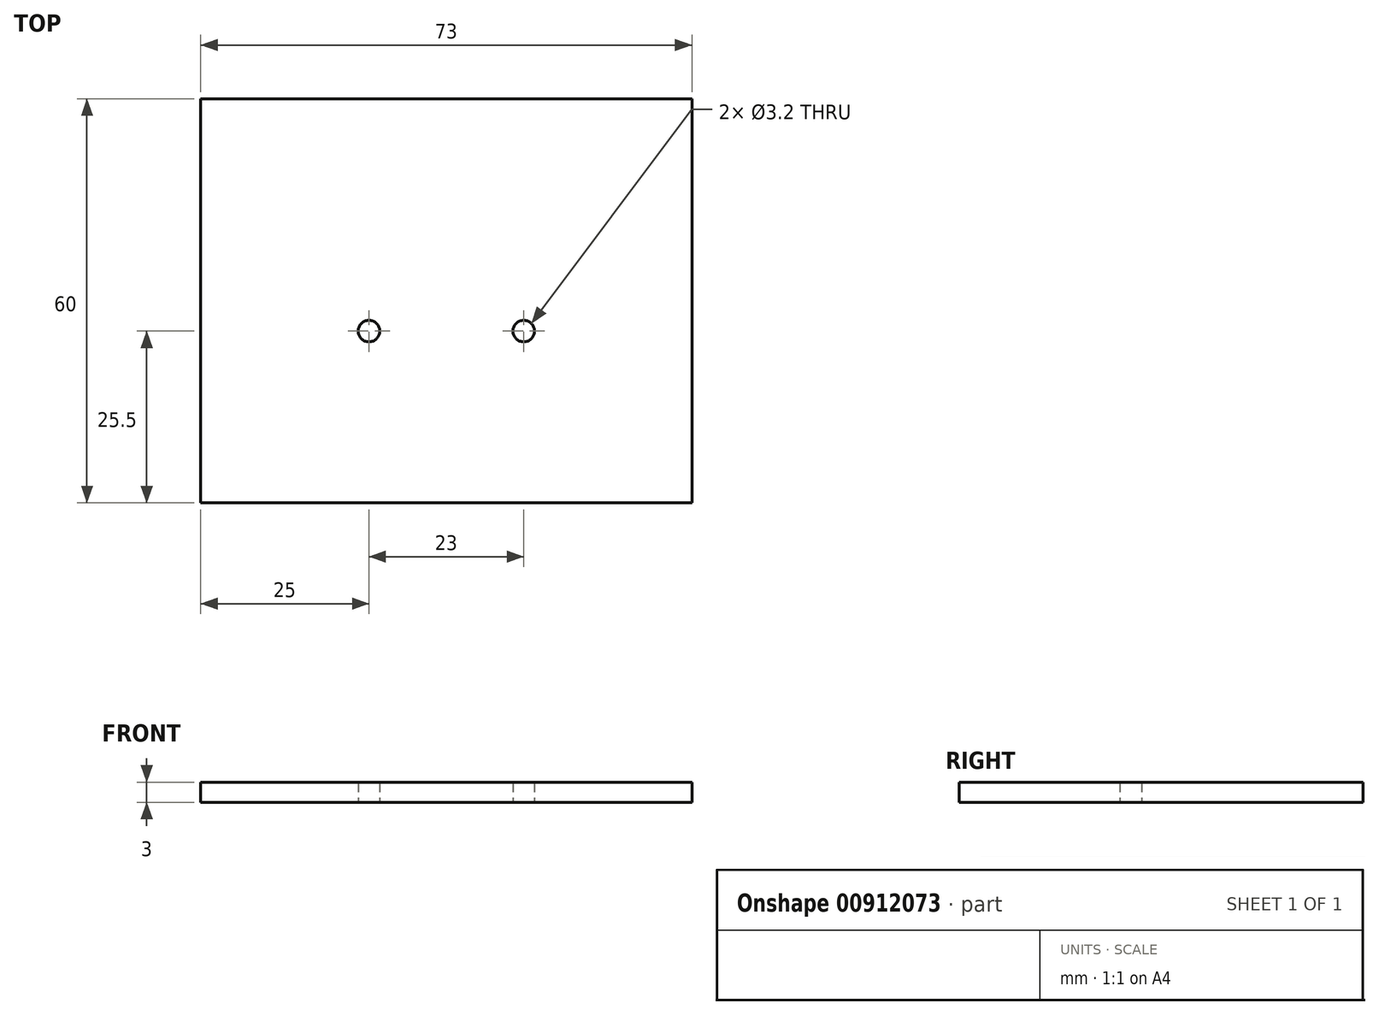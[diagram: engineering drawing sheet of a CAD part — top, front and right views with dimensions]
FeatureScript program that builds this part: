
annotation { "Feature Type Name" : "Feature", "Feature Type Description" : "" }
export const myFeature = defineFeature(function(context is Context, id is Id, definition is map)
    precondition{}
    {
        {
            var Q0;
            Q0=qCreatedBy(makeId("Top.planeOp"),FACE);
            var sketch = newSketch(context, id + "F0", { "sketchPlane" : qUnion([Q0])});
            skLineSegment(sketch, "E0.bottom", {"start": v(-16, -29.1) * mm, "end": v(16, -29.1) * mm});
            skLineSegment(sketch, "E0.top", {"start": v(-16, 30.9) * mm, "end": v(16, 30.9) * mm});
            skCircle(sketch, "E1", {"center": v(-11.5, -3.6) * mm, "radius": 1.6 * mm});
            skCircle(sketch, "E2", {"center": v(11.5, -3.6) * mm, "radius": 1.6 * mm});
            skLineSegment(sketch, "E3", {"start": v(-16, 30.9) * mm, "end": v(-36.5, 30.9) * mm});
            skLineSegment(sketch, "E4", {"start": v(-36.5, 30.9) * mm, "end": v(-36.5, -29.1) * mm});
            skLineSegment(sketch, "E5", {"start": v(-36.5, -29.1) * mm, "end": v(-16, -29.1) * mm});
            skLineSegment(sketch, "E6", {"start": v(16, 30.9) * mm, "end": v(36.5, 30.9) * mm});
            skLineSegment(sketch, "E7", {"start": v(36.5, 30.9) * mm, "end": v(36.5, -29.1) * mm});
            skLineSegment(sketch, "E8", {"start": v(36.5, -29.1) * mm, "end": v(16, -29.1) * mm});
            skSolve(sketch);
        }
        {
            var Q0;
            Q0 = qSketchRegion(id + "F0", true);
            extrude(context, id + "F1", {"entities" : qUnion([Q0]), "depth" : 3 * mm, "offsetDistance" : 25 * mm});
        }
    });
